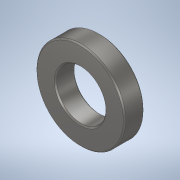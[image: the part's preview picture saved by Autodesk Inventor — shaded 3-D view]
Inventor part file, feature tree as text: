
AUTODESK INVENTOR PART (.ipt)
format: ipt  version: 2022.3 (Build 263350000, 350)  size: 124,928 bytes
history: native  units: in
note: dims shown in document units (in); Inventor stores cm internally (conversion verified against a paired STEP export)
features: extrude x1, chamfer x1, sketch x1
ambient origin geometry x8: Origin, YZ Plane, XZ Plane, XY Plane, X Axis, Y Axis, Z Axis, Center Point
bodies: Solid1 (feature_tree)
feature tree (3):
  extrude  "Extrusion1"  Depth=0.5in
  chamfer  "Chamfer1"  Distance=0.5in
  sketch  "Sketch1"  dims[d0=2.25in d1=1.25in d2=0.5in d3=0.0in d4=0.0312in d5=0.125in d6=45.0deg]
